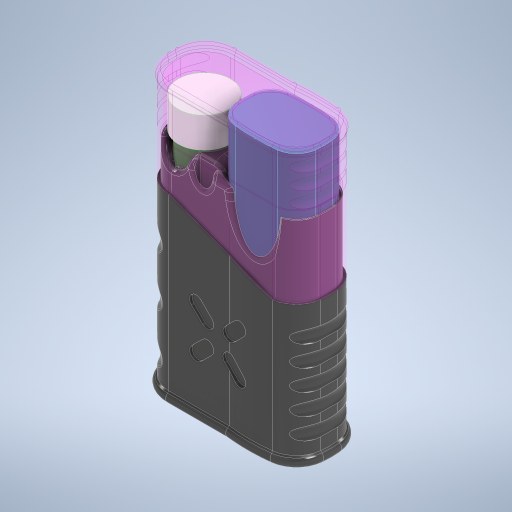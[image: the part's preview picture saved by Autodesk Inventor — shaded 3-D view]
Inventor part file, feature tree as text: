
AUTODESK INVENTOR PART (.ipt)
format: ipt  version: 2023 (Build 270158030, 158C)  size: 3,475,456 bytes
history: native  units: mm
features: fillet x27, sketch x27, extrude x23, projected_geometry x17, other x6, revolve x5, pattern_circular x2, plane x1, sweep x1, mirror x1
ambient origin geometry x8: Origin, YZ Plane, XZ Plane, XY Plane, X Axis, Y Axis, Z Axis, Center Point
bodies: Body1 (feature_tree), Body2 (feature_tree), Body3 (feature_tree), Body4 (feature_tree)
feature tree (110):
  other  "vape"
  extrude  "Extrusion1"  Depth=8.35mm
  fillet  "Fillet1"  Radius=80.0mm
  extrude  "Extrusion2"  Depth=11.6mm TaperAngle=0.0deg
  plane  "Work Plane1"
  extrude  "Extrusion3"  Depth=45.8mm TaperAngle=0.0deg
  extrude  "Extrusion4"  Depth=22.1mm
  extrude  "Extrusion5"  Depth=1.5mm
  extrude  "Extrusion6"  Depth=1.5mm
  fillet  "Fillet2"  Radius=1.5mm
  extrude  "Extrusion8"  Depth=15.55mm
  extrude  "Extrusion20"  Depth=3.0mm
  extrude  "Extrusion21"  Depth=3.0mm
  sweep  "Sweep2"
  sketch  "Sketch26"  dims[d105=71.0mm d106=0.0mm d108=71.0mm d109=0.0mm d110=3.0mm d111=30.0deg]
  extrude  "Extrusion22"  Depth=13.0mm
  fillet  "Fillet22"  Radius=2.0mm
  fillet  "Fillet23"  Radius=10.0mm
  fillet  "Fillet24"  Radius=11.0mm
  fillet  "Fillet25"  Radius=4.0mm
  fillet  "Fillet26"  Radius=2.0mm
  fillet  "Fillet4"  Radius=3.0mm
  extrude  "Extrusion10"  Depth=2.4mm
  extrude  "Extrusion11"  Depth=7.0mm
  fillet  "Fillet10"  Radius=45.0mm
  fillet  "Fillet27"  Radius=0.25mm
  extrude  "Extrusion13"  Depth=71.0mm TaperAngle=0.0deg
  fillet  "Fillet28"  Radius=3.0mm
  sketch  "Sketch14"  dims[d50=3.0mm d51=3.0mm]
  extrude  "Extrusion14"  Depth=15.0mm TaperAngle=0.0deg
  extrude  "Extrusion23"  TaperAngle=0.0deg  [1 undecoded]
  extrude  "Extrusion24"  Depth=15.0mm
  extrude  "Extrusion15"  Depth=20.0mm
  fillet  "Fillet29"  Radius=9.0mm
  extrude  "Extrusion25"  Depth=6.0mm
  fillet  "Fillet30"  Radius=4.0mm
  other  "Work Axis1"
  revolve  "Revolution1"  [1 undecoded]
  sketch  "Sketch30"  dims[d172=15.780931mm d173=20.0mm d174=9.0mm]
  revolve  "Revolution2"  [1 undecoded]
  fillet  "Fillet32"  Radius=1.0mm
  extrude  "Extrusion26"  Depth=2.5mm
  sketch  "Sketch35"  dims[d178=1.0mm d179=2.0mm]
  revolve  "Revolution3"  [1 undecoded]
  revolve  "Revolution5"  [1 undecoded]
  extrude  "Extrusion27"  Depth=10.0mm TaperAngle=0.0deg
  extrude  "Extrusion28"  Depth=6.0mm
  fillet  "Fillet34"  Radius=3.65mm
  other  "Work Axis2"
  revolve  "Revolution6"  [1 undecoded]
  pattern_circular  "Circular Pattern1"  [2 undecoded]
  extrude  "Extrusion29"  Depth=14.0mm
  fillet  "Fillet35"  Radius=19.0mm
  fillet  "Fillet36"  [1 undecoded]
  fillet  "Fillet37"  Radius=8.0mm
  fillet  "Fillet38"  Radius=8.0mm
  fillet  "Fillet39"  Radius=8.0mm
  fillet  "Fillet40"  Radius=8.0mm
  fillet  "Fillet41"  Radius=8.0mm
  pattern_circular  "Circular Pattern2"  [2 undecoded]
  fillet  "Fillet42"  [1 undecoded]
  fillet  "Fillet43"  [1 undecoded]
  fillet  "Fillet44"  Radius=1.5mm
  fillet  "Fillet45"  Radius=0.5mm
  fillet  "Fillet46"  Radius=18.25mm
  extrude  "Extrusion30"  Depth=8.0mm
  mirror  "Mirror1"
  sketch  "Sketch1"  dims[d4=98.5mm d5=0.0mm d9=8.35mm d22=80.0mm d23=0.0mm]
  sketch  "Sketch2"  dims[d24=20.0mm d26=11.6mm d27=0.0mm]
  other  "vape-tube"
  sketch  "Sketch3"  dims[d28=17.0mm d29=45.8mm d30=0.0mm]
  other  "storage"
  sketch  "Sketch4"  dims[d31=17.0mm d38=22.1mm]
  sketch  "Sketch5"  dims[d39=31.1mm d41=1.5mm]
  projected_geometry  "Projected Loop2"
  sketch  "Sketch6"  dims[d42=1.5mm d44=1.5mm d45=1.5mm]
  projected_geometry  "Projected Loop3"
  projected_geometry  "Projected Loop4"
  sketch  "Sketch8"  dims[d46=11.05mm d47=15.55mm]
  projected_geometry  "Projected Loop6"
  sketch  "Sketch11"  dims[d48=3.0mm d49=3.0mm]
  sketch  "Sketch15"  dims[d52=11.05mm d53=15.55mm]
  other  "vape-lid"
  sketch  "Sketch22"  dims[d54=2.0mm d55=13.0mm]
  projected_geometry  "Projected Loop13"
  sketch  "Sketch23"  dims[d56=12.5mm d57=60.0mm d58=0.0mm d59=2.0mm d60=10.0mm d61=0.0mm d62=11.0mm d66=4.0mm d67=8.726646mm d69=2.0mm d83=3.0mm]
  projected_geometry  "Projected Loop14"
  sketch  "Sketch24"  dims[d86=72.0mm d87=0.0mm d88=2.4mm]
  sketch  "Sketch25"  dims[d89=7.3mm d91=7.0mm d92=45.0mm d93=0.0mm d94=0.25mm]
  sketch  "Sketch27"  dims[d158=1.0mm d159=15.0mm d160=0.0mm]
  projected_geometry  "Projected Loop15"
  projected_geometry  "Projected Loop16"
  projected_geometry  "Projected Loop17"
  projected_geometry  "Projected Loop18"
  projected_geometry  "Projected Loop19"
  projected_geometry  "Projected Loop20"
  sketch  "Sketch28"  dims[d161=15.0mm d162=0.0mm d163=0.0mm d164=0.0mm]
  sketch  "Sketch29"  dims[d169=0.0mm d170=0.0mm d171=15.0mm]
  sketch  "Sketch33"  dims[d175=7.5mm d176=6.0mm d177=4.0mm]
  projected_geometry  "Projected Loop31"
  sketch  "Sketch37"  dims[d180=1.2mm d181=0.5mm d182=1.0mm]
  sketch  "Sketch38"  dims[d183=24.0mm d184=2.5mm]
  projected_geometry  "Projected Loop32"
  sketch  "Sketch39"  dims[d185=0.7mm d186=2.35mm]
  projected_geometry  "Projected Loop33"
  projected_geometry  "Projected Loop34"
  projected_geometry  "Projected Loop35"
  sketch  "Sketch40"  dims[d187=4.0mm d188=0.5mm]
  sketch  "Sketch41"  dims[d189=10.0mm d190=0.0mm d191=10.0mm d192=0.0mm]
  sketch  "Sketch44"  dims[d193=1.5mm d194=6.0mm d195=3.65mm d196=10.0mm d197=0.0mm d198=2.5mm d199=14.0mm d200=19.0mm d201=19.0mm d207=180.0deg d208=8.0mm d209=8.0mm d210=8.0mm d211=8.0mm d212=8.0mm d213=12.5mm d215=0.0mm d216=180.0deg d218=1.5mm d220=0.5mm d221=18.25mm d222=0.0mm d223=8.0mm d224=7.0mm d225=6.0mm d226=6.0mm d227=11.5mm d228=6.0mm d229=6.0mm d230=180.0deg d240=3.0mm d241=6.0mm d242=6.0mm d243=6.0mm d244=41.5mm d245=11.5mm d246=6.0mm d247=180.0deg d249=20.0mm d253=22.0mm d254=22.0mm d255=25.0mm d256=1.0mm d257=1.0mm d258=0.0mm d259=1.0mm d260=0.0mm d261=0.2mm d262=11.0mm d263=5.0mm d264=10.0mm d265=2.241222mm d266=10.0mm d267=30.0mm d268=4.0mm d269=45.0deg d270=40.0mm d271=360.0deg d275=0.4mm d276=1.1mm d277=2.4mm d278=3.0mm d279=1.5mm d280=3.0mm d281=0.810487mm d282=2.943591mm d283=4.5mm d284=0.0mm d285=2.0mm d286=0.8mm d287=3.0mm d288=0.5mm d289=1.0mm d290=1.0mm d291=1.0mm d292=40.0mm d293=360.0deg d295=1.0mm d296=0.5mm d297=0.5mm d298=1.0mm d299=0.4mm d309=59.760104mm d310=29.880052mm d311=30.0mm d312=12.0mm d313=45.0deg d315=8.5mm d316=8.5mm d317=5.0mm d318=40.0mm d320=360.0deg d322=10.0mm d323=1.0mm d324=0.0mm d325=0.0mm]
note: 13 required parameter values undecoded (feature->parameter linkage not recoverable at this tier; creation-order binding heuristic only, values carry confidence <= 0.55)